# Revit family: VG_Арматура_УзелНижнегоПодключенияРадиаторов_H-образныйУгловой_VG-606201_VALOGIN
name_source: partatom
category: Арматура трубопроводов
units: mm (PartAtom-declared; Revit-internal decimal feet)

## family parameters
Всегда вертикально = Да
На основе рабочей плоскости = Нет
Общий = Нет
При загрузке вырезать с полостями = Нет
Размер круглого соединителя = Использовать диаметр
Тип детали = Нормальный

## types (1)
- VG_Арматура_УзелНижнегоПодключенияРадиаторов_H-образныйУгловой_VG-606201_VALOGIN
    ADSK_URL документации изделия = https://valogin.technology
    ADSK_URL страницы изделия = https://valogin.technology
    ADSK_Версия Revit = 2019
    ADSK_Версия семейства = v.1.0
    ADSK_Группирование = Радиаторная арматура
    ADSK_Единица измерения = шт.
    ADSK_Завод-изготовитель = VALOGIN
    ADSK_Код изделия = VG-606201
    ADSK_Количество = 1
    ADSK_Марка = VG-606201
    ADSK_Масса = 0.289
    ADSK_Масса_Текст = 0.289
    ADSK_Материал = VG_Металл_Серебро_VALOGIN
    ADSK_Наименование = Узел Н-образный угловой с вентильными затворами для подключения радиаторов в двухтрубных системах отопления
    ADSK_Наименование краткое = Узел Н-образный угловой
    ADSK_Размер_Высота = 33 мм
    ADSK_Размер_Глубина = 28 мм
    ADSK_Размер_Диаметр = 20 мм
    ADSK_Размер_Длина = 83 мм
    BL_BIM library = https://bimlib.pro
    URL = https://valogin.technology
    Изготовитель = VALOGIN
    Максимальная рабочая температура теплоносителя = 120 °C
    Максимальный коэффициент пропускной способности = 1.9 м³/ч
    Номинальное давление = 1.0 МПа
    Описание = Назначение: Н-образные узлы арт. VG-606101 и VG-606201 применяются для подключения отопительных приборов с нижним выходом присоединительных патрубков с соединением типа 3/4" «евроконус» или
внутренней резьбой 1/2" и межосевым расстоянием патрубков 50 мм.
    Пробное давление = 1.5 МПа
    Размер = 3/4"В x 3/4"«евроконус»
    Средний полный срок службы = 20 лет
